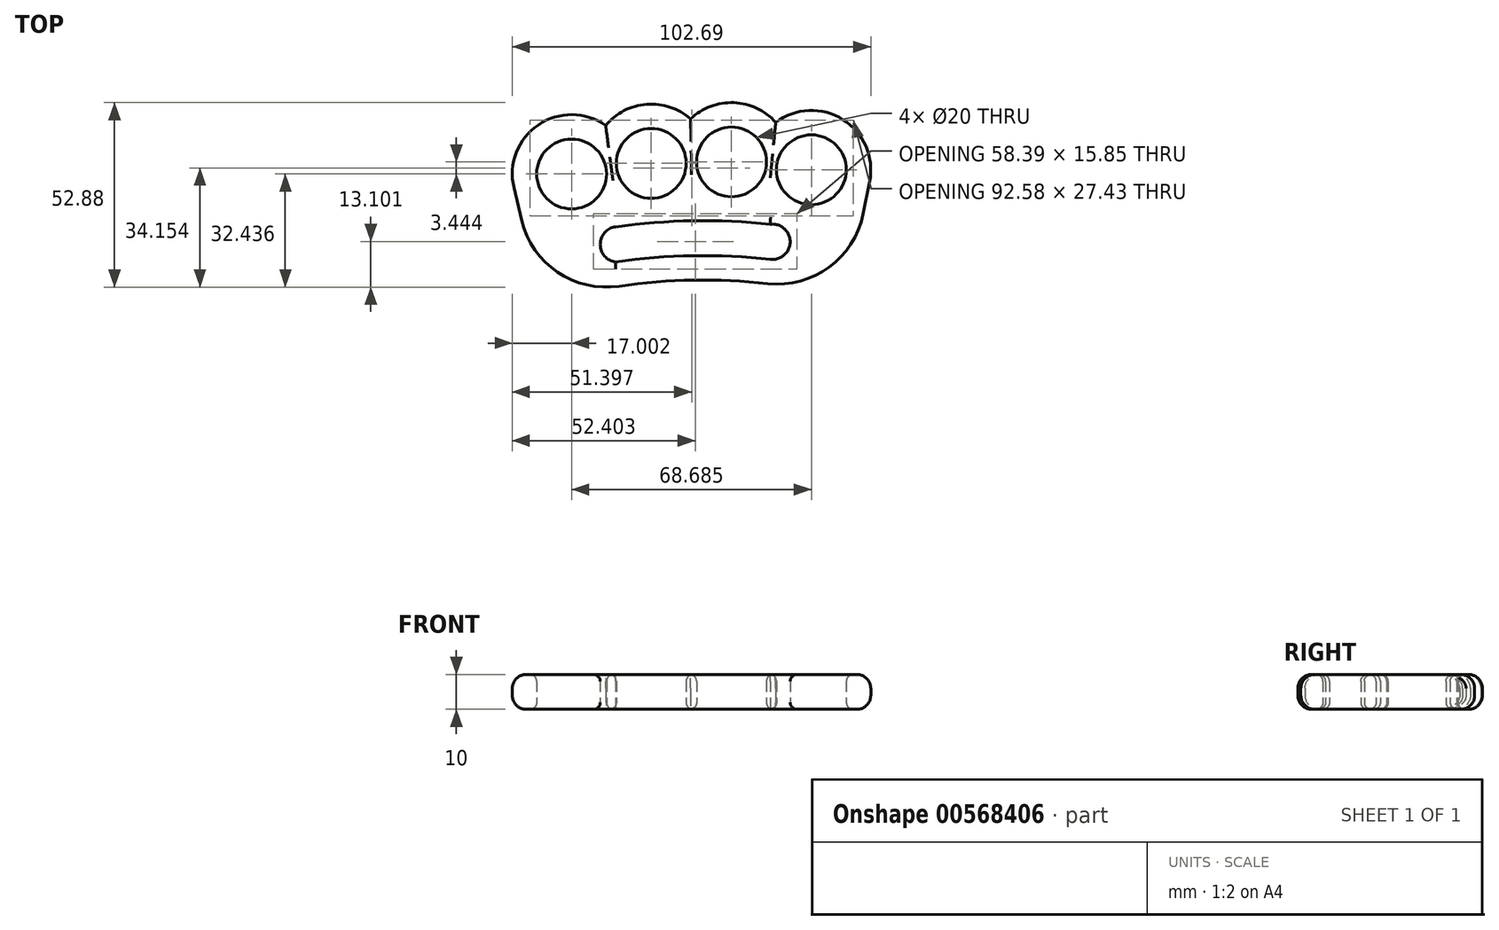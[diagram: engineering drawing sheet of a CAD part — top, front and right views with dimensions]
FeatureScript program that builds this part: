
annotation { "Feature Type Name" : "Feature", "Feature Type Description" : "" }
export const myFeature = defineFeature(function(context is Context, id is Id, definition is map)
    precondition{}
    {
        {
            var Q0;
            Q0=qCreatedBy(makeId("Top.planeOp"),FACE);
            var sketch = newSketch(context, id + "F0", { "sketchPlane" : qUnion([Q0])});
            skCircle(sketch, "E0", {"center": v(-37.8, 151.4) * mm, "radius": 10 * mm});
            skCircle(sketch, "E1", {"center": v(-15, 154.44) * mm, "radius": 10 * mm});
            skCircle(sketch, "E2", {"center": v(8, 154.84) * mm, "radius": 10 * mm});
            skCircle(sketch, "E3", {"center": v(30.89, 152.6) * mm, "radius": 10 * mm});
            skArc(sketch, "E4", {"start": v(-136.24, 101.42) * mm, "mid": v(0.23, 155) * mm, "end": v(136.57, 101.1) * mm, "construction": true});
            skLineSegment(sketch, "E5", {"start": v(0, 0) * mm, "end": v(0, 229.83) * mm, "construction": true});
            skArc(sketch, "E6.0", {"start": v(-24.74, 140.5) * mm, "mid": v(-13.72, 137.48) * mm, "end": v(-3.28, 142.12) * mm, "construction": true});
            skArc(sketch, "E7.trimOffspring", {"start": v(-28.05, 165.33) * mm, "mid": v(-54.65, 149.15) * mm, "end": v(-24.74, 140.5) * mm});
            skArc(sketch, "E8.0", {"start": v(20.66, 166.18) * mm, "mid": v(8.68, 171.83) * mm, "end": v(-3.72, 167.16) * mm});
            skArc(sketch, "E9.trimOffspring", {"start": v(18.22, 141.26) * mm, "mid": v(47.8, 150.95) * mm, "end": v(20.66, 166.18) * mm});
            skArc(sketch, "E10.trimOffspring", {"start": v(-3.72, 167.16) * mm, "mid": v(-16.28, 171.39) * mm, "end": v(-28.05, 165.33) * mm});
            skArc(sketch, "E11.trimOffspring", {"start": v(-3.28, 142.12) * mm, "mid": v(7.32, 137.85) * mm, "end": v(18.22, 141.26) * mm, "construction": true});
            skArc(sketch, "E12.0", {"start": v(-24.17, 119.23) * mm, "mid": v(-2.91, 120.97) * mm, "end": v(18.4, 119.98) * mm});
            skPoint(sketch, "E13.startSnap0", {"position": v(-54.65, 149.15) * mm});
            skLineSegment(sketch, "E14", {"start": v(47.56, 149.26) * mm, "end": v(45.69, 139.92) * mm});
            skLineSegment(sketch, "E15", {"start": v(-54.34, 147.48) * mm, "end": v(-52.14, 138.2) * mm});
            skPoint(sketch, "E16.visualSharp", {"position": v(-46.5, 114.36) * mm});
            skArc(sketch, "E16.filletArc", {"start": v(-52.14, 138.2) * mm, "mid": v(-41.85, 123.27) * mm, "end": v(-24.17, 119.23) * mm});
            skPoint(sketch, "E17.visualSharp", {"position": v(40.88, 115.89) * mm});
            skArc(sketch, "E17.filletArc", {"start": v(18.4, 119.98) * mm, "mid": v(35.92, 124.64) * mm, "end": v(45.69, 139.92) * mm});
            skLineSegment(sketch, "E18.0", {"start": v(19.18, 126.93) * mm, "end": v(19.18, 126.93) * mm});
            skArc(sketch, "E18.1", {"start": v(-25.2, 126.16) * mm, "mid": v(-3.03, 127.97) * mm, "end": v(19.18, 126.93) * mm});
            skLineSegment(sketch, "E18.2", {"start": v(-25.2, 126.16) * mm, "end": v(-25.2, 126.16) * mm});
            skArc(sketch, "E19.0", {"start": v(-25.2, 136.26) * mm, "mid": v(-3.03, 137.97) * mm, "end": v(19.18, 137) * mm});
            skPoint(sketch, "E20.visualSharp", {"position": v(-42.15, 133.08) * mm});
            skPoint(sketch, "E21.visualSharp", {"position": v(35.88, 134.45) * mm});
            skLineSegment(sketch, "E22", {"start": v(-25.2, 126.16) * mm, "end": v(-25.2, 151.27) * mm, "construction": true});
            skArc(sketch, "E23", {"start": v(-25.2, 136.26) * mm, "mid": v(-29.6, 131.2) * mm, "end": v(-25.2, 126.16) * mm});
            skLineSegment(sketch, "E24", {"start": v(19.18, 126.93) * mm, "end": v(19.18, 137) * mm, "construction": true});
            skArc(sketch, "E25", {"start": v(19.18, 126.93) * mm, "mid": v(24.8, 131.96) * mm, "end": v(19.18, 137) * mm});
            skSolve(sketch);
        }
        {
            var Q0;
            Q0=makeQuery(id+"F0.imprint","IMPRINT",FACE,{"disambiguationData":[TD([[makeQuery(id+"F0.imprint","IMPRINT",EDGE,{"derivedFrom":sQuery(id+"F0.wireOp",EDGE,"E0")}),-1.0]])]});
            extrude(context, id + "F1", {"entities" : qUnion([Q0]), "depth" : 10 * mm, "offsetDistance" : 25 * mm});
        }
        {
            var Q0;
            Q0=makeQuery(id+"F1.opExtrude","CAP_EDGE",EDGE,{"disambiguationData":[OSD([sQuery(id+"F0.wireOp",EDGE,"E16.filletArc")])],"isStart":false});
            var Q1;
            Q1=makeQuery(id+"F1.opExtrude","CAP_EDGE",EDGE,{"disambiguationData":[OSD([sQuery(id+"F0.wireOp",EDGE,"E15")])],"isStart":true});
            var Q2;
            Q2=makeQuery(id+"F1.opExtrude","CAP_EDGE",EDGE,{"disambiguationData":[OSD([sQuery(id+"F0.wireOp",EDGE,"E10.trimOffspring")])],"isStart":true});
            var Q3;
            Q3=makeQuery(id+"F1.opExtrude","CAP_EDGE",EDGE,{"disambiguationData":[OSD([sQuery(id+"F0.wireOp",EDGE,"E8.0")])],"isStart":true});
            var Q4;
            Q4=makeQuery(id+"F1.opExtrude","CAP_EDGE",EDGE,{"disambiguationData":[OSD([sQuery(id+"F0.wireOp",EDGE,"E10.trimOffspring")])],"isStart":false});
            var Q5;
            Q5=makeQuery(id+"F1.opExtrude","CAP_EDGE",EDGE,{"disambiguationData":[OSD([sQuery(id+"F0.wireOp",EDGE,"E8.0")])],"isStart":false});
            fillet(context, id + "F2", {"entities" : qUnion([Q0, Q1, Q2, Q3, Q4, Q5]), "radius" : 4 * mm, "tangentPropagation" : true, "allowEdgeOverflow" : false});
        }
        {
            var Q0;
            Q0=makeQuery(id+"F1.opExtrude","CAP_EDGE",EDGE,{"disambiguationData":[OSD([sQuery(id+"F0.wireOp",EDGE,"E2")])],"isStart":false});
            var Q1;
            Q1=makeQuery(id+"F1.opExtrude","CAP_EDGE",EDGE,{"disambiguationData":[OSD([sQuery(id+"F0.wireOp",EDGE,"E1")])],"isStart":false});
            var Q2;
            Q2=makeQuery(id+"F1.opExtrude","CAP_EDGE",EDGE,{"disambiguationData":[OSD([sQuery(id+"F0.wireOp",EDGE,"E0")])],"isStart":false});
            var Q3;
            Q3=makeQuery(id+"F1.opExtrude","CAP_EDGE",EDGE,{"disambiguationData":[OSD([sQuery(id+"F0.wireOp",EDGE,"E3")])],"isStart":false});
            var Q4;
            Q4=makeQuery(id+"F1.opExtrude","CAP_EDGE",EDGE,{"disambiguationData":[OSD([sQuery(id+"F0.wireOp",EDGE,"E0")])],"isStart":true});
            var Q5;
            Q5=makeQuery(id+"F1.opExtrude","CAP_EDGE",EDGE,{"disambiguationData":[OSD([sQuery(id+"F0.wireOp",EDGE,"E1")])],"isStart":true});
            var Q6;
            Q6=makeQuery(id+"F1.opExtrude","CAP_EDGE",EDGE,{"disambiguationData":[OSD([sQuery(id+"F0.wireOp",EDGE,"E2")])],"isStart":true});
            var Q7;
            Q7=makeQuery(id+"F1.opExtrude","CAP_EDGE",EDGE,{"disambiguationData":[OSD([sQuery(id+"F0.wireOp",EDGE,"E3")])],"isStart":true});
            fillet(context, id + "F3", {"entities" : qUnion([Q0, Q1, Q2, Q3, Q4, Q5, Q6, Q7]), "radius" : 2 * mm, "tangentPropagation" : true, "allowEdgeOverflow" : false});
        }
        {
            var Q0;
            Q0=makeQuery(id+"F1.opExtrude","CAP_EDGE",EDGE,{"disambiguationData":[OSD([sQuery(id+"F0.wireOp",EDGE,"E25")])],"isStart":false});
            var Q1;
            Q1=makeQuery(id+"F1.opExtrude","CAP_EDGE",EDGE,{"disambiguationData":[OSD([sQuery(id+"F0.wireOp",EDGE,"E23")])],"isStart":false});
            var Q2;
            Q2=makeQuery(id+"F1.opExtrude","CAP_EDGE",EDGE,{"disambiguationData":[OSD([sQuery(id+"F0.wireOp",EDGE,"E18.1")])],"isStart":false});
            var Q3;
            Q3=makeQuery(id+"F1.opExtrude","CAP_EDGE",EDGE,{"disambiguationData":[OSD([sQuery(id+"F0.wireOp",EDGE,"E19.0")])],"isStart":false});
            var Q4;
            Q4=makeQuery(id+"F1.opExtrude","CAP_EDGE",EDGE,{"disambiguationData":[OSD([sQuery(id+"F0.wireOp",EDGE,"E25")])],"isStart":true});
            var Q5;
            Q5=makeQuery(id+"F1.opExtrude","CAP_EDGE",EDGE,{"disambiguationData":[OSD([sQuery(id+"F0.wireOp",EDGE,"E18.1")])],"isStart":true});
            var Q6;
            Q6=makeQuery(id+"F1.opExtrude","CAP_FACE",FACE,{"disambiguationData":[OSD([sQuery(id+"F0.wireOp",EDGE,"E0"),sQuery(id+"F0.wireOp",EDGE,"E1"),sQuery(id+"F0.wireOp",EDGE,"E2"),sQuery(id+"F0.wireOp",EDGE,"E3"),sQuery(id+"F0.wireOp",EDGE,"E7.trimOffspring"),sQuery(id+"F0.wireOp",EDGE,"E8.0"),sQuery(id+"F0.wireOp",EDGE,"E9.trimOffspring"),sQuery(id+"F0.wireOp",EDGE,"E10.trimOffspring"),sQuery(id+"F0.wireOp",EDGE,"E12.0"),sQuery(id+"F0.wireOp",EDGE,"E14"),sQuery(id+"F0.wireOp",EDGE,"E15"),sQuery(id+"F0.wireOp",EDGE,"E16.filletArc"),sQuery(id+"F0.wireOp",EDGE,"E17.filletArc"),sQuery(id+"F0.wireOp",EDGE,"E18.1"),sQuery(id+"F0.wireOp",EDGE,"E19.0"),sQuery(id+"F0.wireOp",EDGE,"E23"),sQuery(id+"F0.wireOp",EDGE,"E25")])],"isStart":true});
            fillet(context, id + "F4", {"entities" : qUnion([Q0, Q1, Q2, Q3, Q4, Q5, Q6]), "radius" : 2 * mm, "allowEdgeOverflow" : false});
        }
    });
